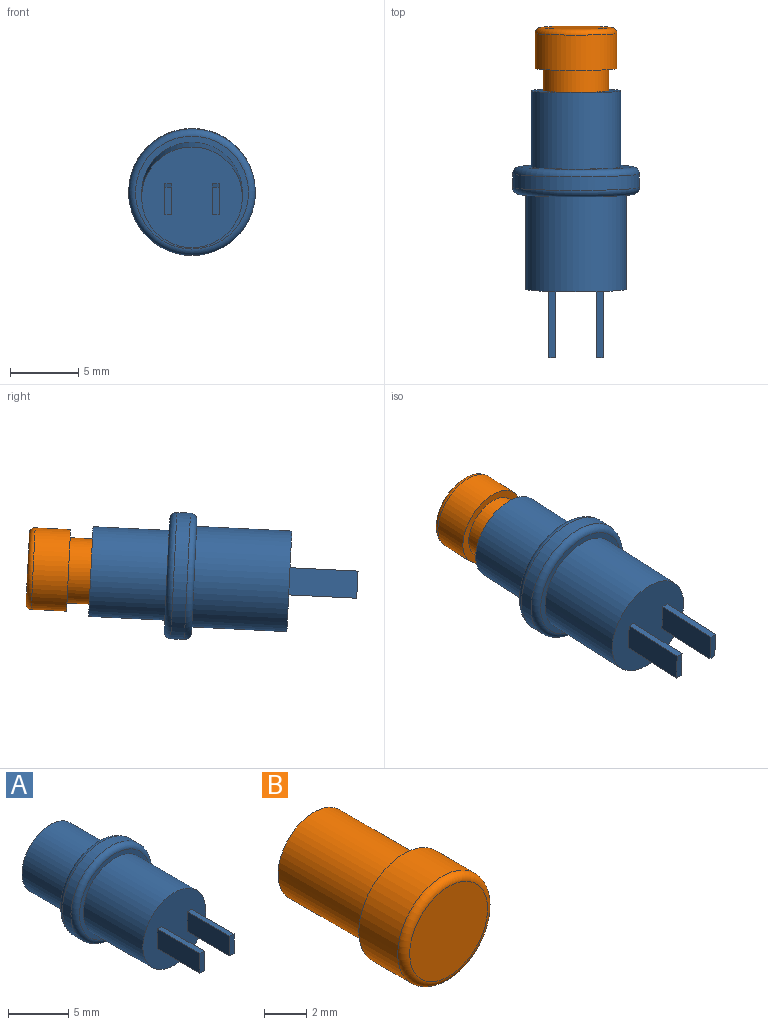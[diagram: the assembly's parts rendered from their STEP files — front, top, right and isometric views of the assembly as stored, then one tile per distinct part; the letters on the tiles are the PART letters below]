
ASSEMBLY  parts=2 mates=1
PART A: 21 faces, bbox 10.1x19.6x10.1 mm
  f0: plane 7.4x7.4mm, normal (0,-1,0), area 41mm2, adj f9,f11,f12,f13,f14,f16,f17,f18
  f1: cylinder r=2.4mm len=7.6mm, axis (0,1,0), area 114.6mm2, adj f3,f10
  f2: cylinder r=3.3mm len=6.6mm, axis (0,1,0), area 116.1mm2, adj f3,f6
  f3: plane 6.6x6.6mm, normal (0,1,0), area 16.1mm2, adj f1,f2
  f4: cylinder r=4.65mm len=9.3mm, axis (0,1,0), area 29.2mm2, adj f7,f8
  f5: plane 8.3x8.3mm, normal (0,-1,0), area 11.1mm2, adj f8,f9
  f6: plane 8.3x8.3mm, normal (0,1,0), area 19.9mm2, adj f2,f7
  f7: torus R=4.15mm, axis (0,-1,0), area 22.1mm2, adj f4,f6
  f8: torus R=4.15mm, axis (0,-1,0), area 22.1mm2, adj f4,f5
  f9: cylinder r=3.7mm len=7.4mm, axis (0,1,0), area 162.7mm2, adj f0,f5
  f10: plane 4.8x4.8mm, normal (0,1,0), area 18.1mm2, adj f1
  f11: plane 5x0.5mm, normal (0,0,1), area 2.5mm2, adj f0,f12,f14,f15
  f12: plane 5x2mm, normal (-1,0,0), area 10mm2, adj f0,f11,f13,f15
  f13: plane 5x0.5mm, normal (0,0,-1), area 2.5mm2, adj f0,f12,f14,f15
  f14: plane 5x2mm, normal (1,0,0), area 10mm2, adj f0,f11,f13,f15
  f15: plane 2x0.5mm, normal (0,-1,0), area 1mm2, adj f11,f12,f13,f14
  f16: plane 5x0.5mm, normal (0,0,1), area 2.5mm2, adj f0,f17,f19,f20
  f17: plane 5x2mm, normal (-1,0,0), area 10mm2, adj f0,f16,f18,f20
  f18: plane 5x0.5mm, normal (0,0,-1), area 2.5mm2, adj f0,f17,f19,f20
  f19: plane 5x2mm, normal (1,0,0), area 10mm2, adj f0,f16,f18,f20
  f20: plane 2x0.5mm, normal (0,-1,0), area 1mm2, adj f16,f17,f18,f19
PART B: 6 faces, bbox 6.5x9x6.5 mm
  f0: cylinder r=2.4mm len=6mm, axis (0,-1,0), area 90.5mm2, adj f1,f4
  f1: plane 4.8x4.8mm, normal (0,1,0), area 18.1mm2, adj f0
  f2: cylinder r=3mm len=6mm, axis (0,1,0), area 49mm2, adj f4,f5
  f3: plane 5.2x5.2mm, normal (0,-1,0), area 21.2mm2, adj f5
  f4: plane 6x6mm, normal (0,1,0), area 10.2mm2, adj f0,f2
  f5: torus R=2.6mm, axis (0,-1,0), area 11.3mm2, adj f2,f3
PLACE A rot(axis=(1,0,0),2.8deg) t=(19.44,2.24,1.06)mm
PLACE B rot(axis=(-1,0,0),177.2deg) t=(19.44,3.88,1.14)mm
MATE slider A.f1 <-> B.f0  axis (0,1,0.05) through (19.44,2.24,1.06)mm
